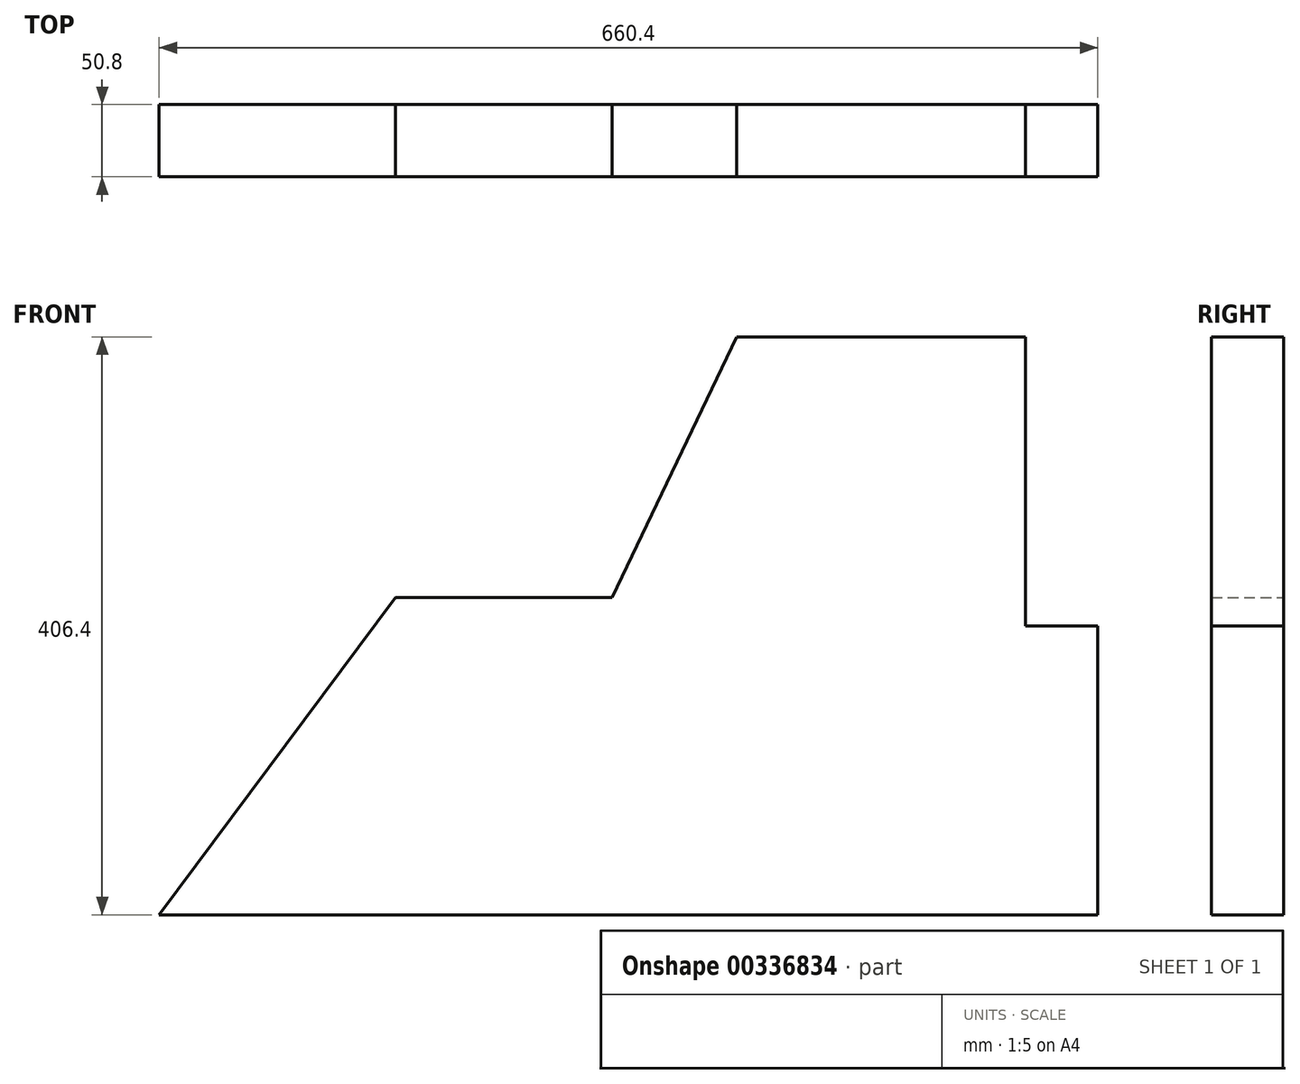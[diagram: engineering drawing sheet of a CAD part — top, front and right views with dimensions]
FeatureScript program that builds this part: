
annotation { "Feature Type Name" : "Feature", "Feature Type Description" : "" }
export const myFeature = defineFeature(function(context is Context, id is Id, definition is map)
    precondition{}
    {
        {
            var Q0;
            Q0=qCreatedBy(makeId("Front.planeOp"),FACE);
            var sketch = newSketch(context, id + "F0", { "sketchPlane" : qUnion([Q0])});
            skLineSegment(sketch, "E0", {"start": v(328.3, 183.37) * mm, "end": v(125.1, 183.37) * mm});
            skLineSegment(sketch, "E1", {"start": v(328.3, 183.37) * mm, "end": v(328.3, -19.83) * mm});
            skLineSegment(sketch, "E2", {"start": v(328.3, -19.83) * mm, "end": v(379.1, -19.83) * mm});
            skLineSegment(sketch, "E3", {"start": v(379.1, -223.03) * mm, "end": v(-281.3, -223.03) * mm});
            skLineSegment(sketch, "E4", {"start": v(379.1, -19.83) * mm, "end": v(379.1, -223.03) * mm});
            skLineSegment(sketch, "E5", {"start": v(125.1, 183.37) * mm, "end": v(37.5, 0) * mm});
            skLineSegment(sketch, "E6", {"start": v(37.5, 0) * mm, "end": v(-114.9, 0) * mm});
            skLineSegment(sketch, "E7", {"start": v(-114.9, 0) * mm, "end": v(-281.3, -223.03) * mm});
            skSolve(sketch);
        }
        {
            var Q0;
            Q0=makeQuery(id+"F0.imprint","IMPRINT",FACE,{"disambiguationData":[TD([[makeQuery(id+"F0.imprint","IMPRINT",EDGE,{"derivedFrom":sQuery(id+"F0.wireOp",EDGE,"E0")}),1.0]])]});
            extrude(context, id + "F1", {"entities" : qUnion([Q0]), "depth" : 50.8 * mm});
        }
    });
